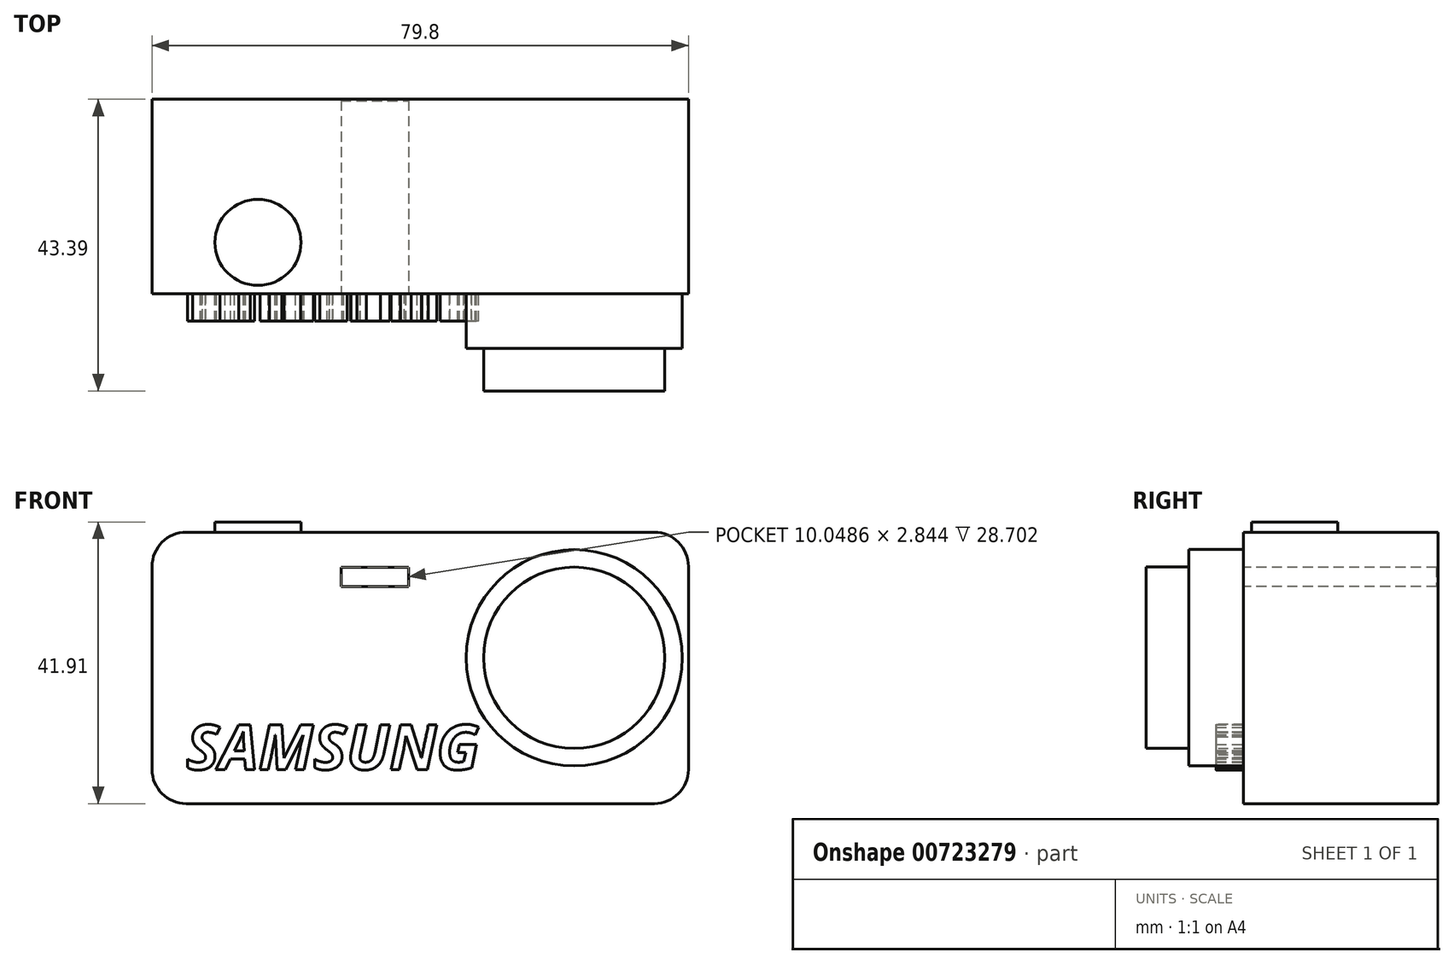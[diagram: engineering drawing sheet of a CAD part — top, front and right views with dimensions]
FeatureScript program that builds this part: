
annotation { "Feature Type Name" : "Feature", "Feature Type Description" : "" }
export const myFeature = defineFeature(function(context is Context, id is Id, definition is map)
    precondition{}
    {
        {
            var Q0;
            Q0=qCreatedBy(makeId("Top.planeOp"),FACE);
            var sketch = newSketch(context, id + "F0", { "sketchPlane" : qUnion([Q0])});
            skLineSegment(sketch, "E0.bottom", {"start": v(-20.06, 0) * mm, "end": v(59.74, 0) * mm});
            skLineSegment(sketch, "E0.top", {"start": v(-20.06, 28.9) * mm, "end": v(59.74, 28.9) * mm});
            skLineSegment(sketch, "E0.left", {"start": v(-20.06, 0) * mm, "end": v(-20.06, 28.9) * mm});
            skLineSegment(sketch, "E0.right", {"start": v(59.74, 0) * mm, "end": v(59.74, 28.9) * mm});
            skSolve(sketch);
        }
        {
            var Q0;
            Q0 = qSketchRegion(id + "F0", true);
            extrude(context, id + "F1", {"entities" : qUnion([Q0]), "depth" : 40.4 * mm, "offsetDistance" : 25.4 * mm});
        }
        {
            var Q0;
            Q0=makeQuery(id+"F1.opExtrude","SWEPT_FACE",FACE,{"disambiguationData":[OSD([sQuery(id+"F0.wireOp",EDGE,"E0.bottom")])]});
            var sketch = newSketch(context, id + "F2", { "sketchPlane" : qUnion([Q0])});
            skCircle(sketch, "E1", {"center": v(42.75, 21.7) * mm, "radius": 16.1 * mm});
            skSolve(sketch);
        }
        {
            var Q0;
            Q0 = qSketchRegion(id + "F2", true);
            extrude(context, id + "F3", {"entities" : qUnion([Q0]), "operationType" : NewBodyOperationType.ADD, "depth" : 8.13 * mm, "offsetDistance" : 25.4 * mm});
        }
        {
            var Q0;
            Q0=makeQuery(id+"F1.opExtrude","CAP_EDGE",EDGE,{"disambiguationData":[OSD([sQuery(id+"F0.wireOp",EDGE,"E0.left")])],"isStart":false});
            var Q1;
            Q1=makeQuery(id+"F1.opExtrude","CAP_EDGE",EDGE,{"disambiguationData":[OSD([sQuery(id+"F0.wireOp",EDGE,"E0.left")])],"isStart":true});
            var Q2;
            Q2=makeQuery(id+"F1.opExtrude","CAP_EDGE",EDGE,{"disambiguationData":[OSD([sQuery(id+"F0.wireOp",EDGE,"E0.right")])],"isStart":false});
            var Q3;
            Q3=makeQuery(id+"F1.opExtrude","CAP_EDGE",EDGE,{"disambiguationData":[OSD([sQuery(id+"F0.wireOp",EDGE,"E0.right")])],"isStart":true});
            fillet(context, id + "F4", {"entities" : qUnion([Q0, Q1, Q2, Q3]), "radius" : 5.08 * mm, "tangentPropagation" : true, "allowEdgeOverflow" : false});
        }
        {
            var Q0;
            Q0=makeQuery(id+"F3.opExtrude","CAP_FACE",FACE,{"disambiguationData":[OSD([sQuery(id+"F2.wireOp",EDGE,"E1")])],"isStart":false});
            var sketch = newSketch(context, id + "F5", { "sketchPlane" : qUnion([Q0])});
            skCircle(sketch, "E2", {"center": v(42.75, 21.7) * mm, "radius": 13.49 * mm});
            skSolve(sketch);
        }
        {
            var Q0;
            Q0 = qSketchRegion(id + "F5", true);
            extrude(context, id + "F6", {"entities" : qUnion([Q0]), "operationType" : NewBodyOperationType.ADD, "depth" : 6.35 * mm, "offsetDistance" : 25.4 * mm});
        }
        {
            var Q0;
            Q0=makeQuery(id+"F6.opExtrude","CAP_FACE",FACE,{"disambiguationData":[OSD([sQuery(id+"F5.wireOp",EDGE,"E2")])],"isStart":false});
            var sketch = newSketch(context, id + "F7", { "sketchPlane" : qUnion([Q0])});
            skCircle(sketch, "E3", {"center": v(42.75, 21.7) * mm, "radius": 9.74 * mm});
            skSolve(sketch);
        }
        {
            var Q0;
            Q0 = qSketchRegion(id + "F7", true);
            extrude(context, id + "F8", {"entities" : qUnion([Q0]), "operationType" : NewBodyOperationType.ADD, "oppositeDirection" : true, "depth" : 25.4 * mm, "offsetDistance" : 25.4 * mm});
        }
        {
            var Q0;
            Q0=makeQuery(id+"F1.opExtrude","SWEPT_FACE",FACE,{"disambiguationData":[OSD([sQuery(id+"F0.wireOp",EDGE,"E0.bottom")])]});
            var sketch = newSketch(context, id + "F9", { "sketchPlane" : qUnion([Q0])});
            skText(sketch, "E4", { "text": "SAMSUNG", "fontName": "OpenSans-BoldItalic.ttf"});
            const initialGuessF9  = {"E4": [-0.01498, 0.00508, 1, 0, 0.00668]};
            skSetInitialGuess(sketch, initialGuessF9);
            skSolve(sketch);
        }
        {
            var Q0;
            Q0 = qSketchRegion(id + "F9", true);
            extrude(context, id + "F10", {"entities" : qUnion([Q0]), "operationType" : NewBodyOperationType.ADD, "depth" : 4.06 * mm, "offsetDistance" : 25.4 * mm});
        }
        {
            var Q0;
            {var subQ1=sQuery(id+"F0.wireOp",EDGE,"E0.left");var subQ3=sQuery(id+"F0.wireOp",EDGE,"E0.bottom");Q0=makeQuery(id+"F10.boolean.opBoolean","SPLIT",FACE,{"disambiguationData":[TD([makeQuery(id+"F1.opExtrude","SWEPT_FACE",FACE,{"disambiguationData":[OSD([subQ1])]})])],"derivedFrom":makeQuery(id+"F1.opExtrude","SWEPT_FACE",FACE,{"disambiguationData":[OSD([subQ3])]})});}
            var sketch = newSketch(context, id + "F11", { "sketchPlane" : qUnion([Q0])});
            skLineSegment(sketch, "E5.bottom", {"start": v(8.06, 35.17) * mm, "end": v(18.1, 35.17) * mm});
            skLineSegment(sketch, "E5.top", {"start": v(8.06, 32.33) * mm, "end": v(18.1, 32.33) * mm});
            skLineSegment(sketch, "E5.left", {"start": v(8.06, 35.17) * mm, "end": v(8.06, 32.33) * mm});
            skLineSegment(sketch, "E5.right", {"start": v(18.1, 35.17) * mm, "end": v(18.1, 32.33) * mm});
            skSolve(sketch);
        }
        {
            var Q0;
            Q0 = qSketchRegion(id + "F11", true);
            extrude(context, id + "F12", {"entities" : qUnion([Q0]), "operationType" : NewBodyOperationType.REMOVE, "oppositeDirection" : true, "depth" : 28.7 * mm, "offsetDistance" : 25.4 * mm});
        }
        {
            var Q0;
            Q0=makeQuery(id+"F1.opExtrude","CAP_FACE",FACE,{"disambiguationData":[OSD([sQuery(id+"F0.wireOp",EDGE,"E0.bottom"),sQuery(id+"F0.wireOp",EDGE,"E0.top"),sQuery(id+"F0.wireOp",EDGE,"E0.left"),sQuery(id+"F0.wireOp",EDGE,"E0.right")])],"isStart":false});
            var sketch = newSketch(context, id + "F13", { "sketchPlane" : qUnion([Q0])});
            skCircle(sketch, "E6", {"center": v(-4.3, 7.62) * mm, "radius": 6.4 * mm});
            skSolve(sketch);
        }
        {
            var Q0;
            Q0=makeQuery(id+"F13.imprint","IMPRINT",FACE,{"disambiguationData":[TD([[makeQuery(id+"F13.imprint","IMPRINT",EDGE,{"derivedFrom":sQuery(id+"F13.wireOp",EDGE,"E6")}),1.0]])]});
            extrude(context, id + "F14", {"entities" : qUnion([Q0]), "operationType" : NewBodyOperationType.ADD, "depth" : 1.52 * mm, "offsetDistance" : 25.4 * mm});
        }
    });
